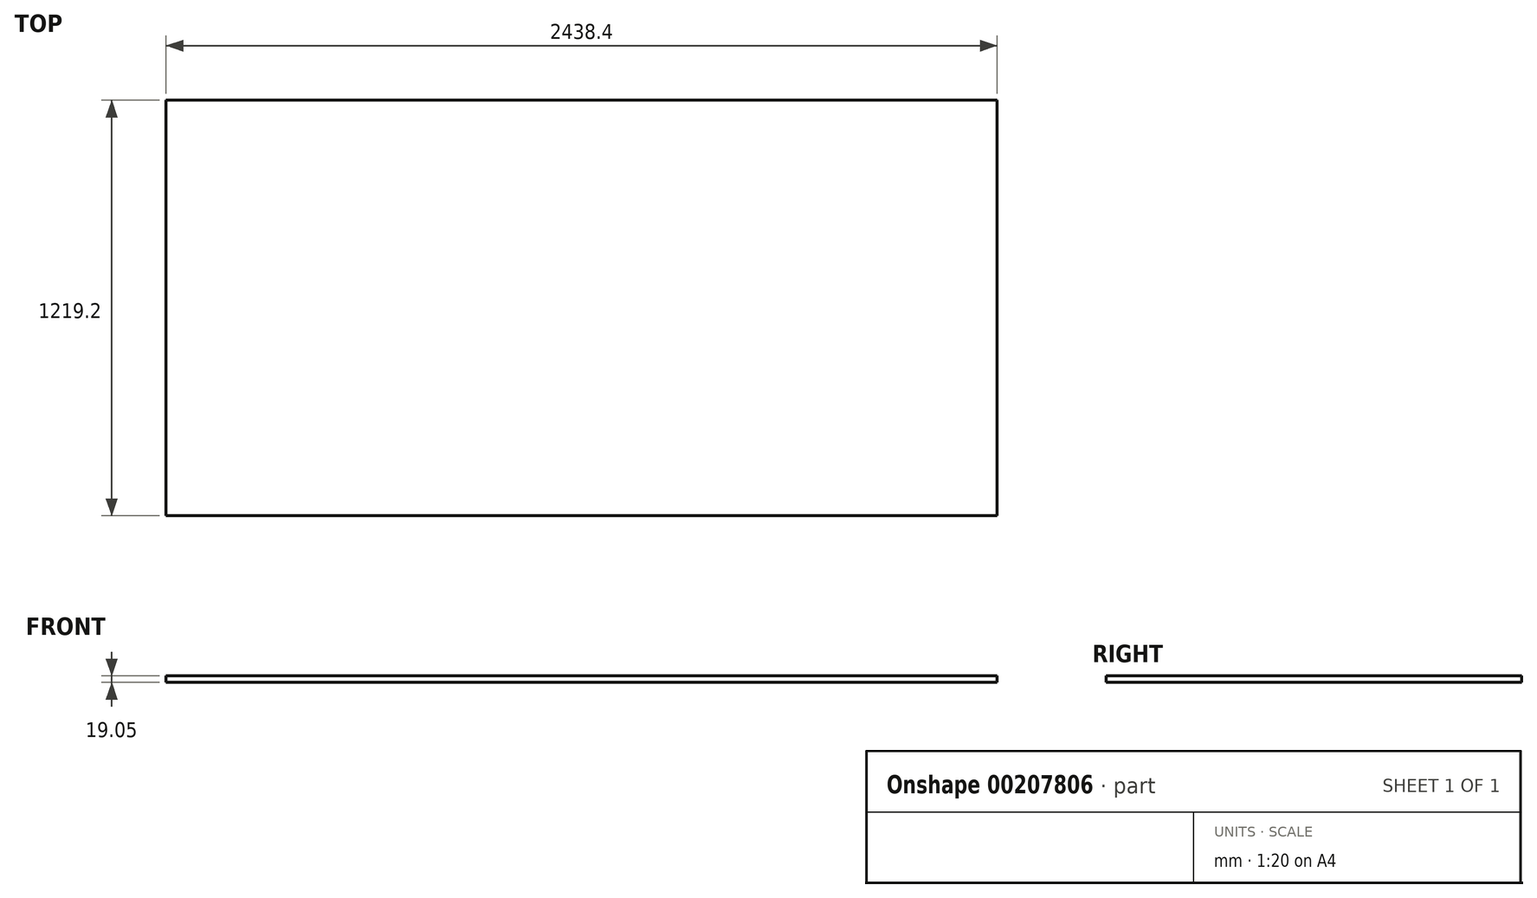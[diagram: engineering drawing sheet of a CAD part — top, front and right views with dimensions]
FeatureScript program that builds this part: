
annotation { "Feature Type Name" : "Feature", "Feature Type Description" : "" }
export const myFeature = defineFeature(function(context is Context, id is Id, definition is map)
    precondition{}
    {
        {
            var Q0;
            Q0=qCreatedBy(makeId("Top.planeOp"),FACE);
            var sketch = newSketch(context, id + "F0", { "sketchPlane" : qUnion([Q0])});
            skLineSegment(sketch, "E0.bottom", {"start": v(0, 0) * mm, "end": v(2438.4, 0) * mm});
            skLineSegment(sketch, "E0.top", {"start": v(0, 1219.2) * mm, "end": v(2438.4, 1219.2) * mm});
            skLineSegment(sketch, "E0.left", {"start": v(0, 0) * mm, "end": v(0, 1219.2) * mm});
            skLineSegment(sketch, "E0.right", {"start": v(2438.4, 0) * mm, "end": v(2438.4, 1219.2) * mm});
            skSolve(sketch);
        }
        {
            var Q0;
            Q0=makeQuery(id+"F0.imprint","IMPRINT",FACE,{"disambiguationData":[TD([[makeQuery(id+"F0.imprint","IMPRINT",EDGE,{"derivedFrom":sQuery(id+"F0.wireOp",EDGE,"E0.bottom")}),1.0]])]});
            extrude(context, id + "F1", {"entities" : qUnion([Q0]), "depth" : 19.05 * mm});
        }
    });
